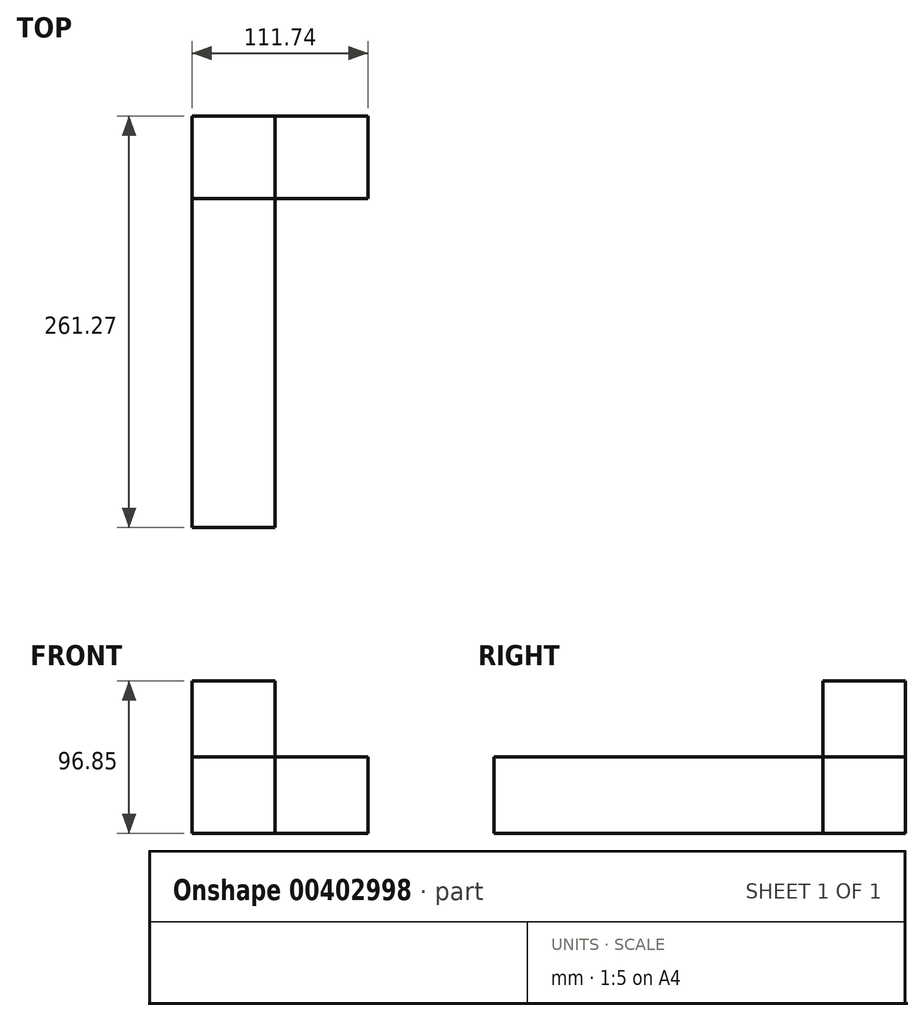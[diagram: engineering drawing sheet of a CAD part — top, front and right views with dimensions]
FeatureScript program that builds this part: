
annotation { "Feature Type Name" : "Feature", "Feature Type Description" : "" }
export const myFeature = defineFeature(function(context is Context, id is Id, definition is map)
    precondition{}
    {
        {
            var Q0;
            Q0=qCreatedBy(makeId("Top.planeOp"),FACE);
            var sketch = newSketch(context, id + "F0", { "sketchPlane" : qUnion([Q0])});
            skLineSegment(sketch, "E0.bottom", {"start": v(0, 0) * mm, "end": v(52.76, 0) * mm});
            skLineSegment(sketch, "E0.top", {"start": v(0, 52.48) * mm, "end": v(52.76, 52.48) * mm});
            skLineSegment(sketch, "E0.left", {"start": v(0, 0) * mm, "end": v(0, 52.48) * mm});
            skLineSegment(sketch, "E0.right", {"start": v(52.76, 0) * mm, "end": v(52.76, 52.48) * mm});
            skSolve(sketch);
        }
        {
            var Q0;
            Q0=makeQuery(id+"F0.imprint","IMPRINT",FACE,{"disambiguationData":[TD([[makeQuery(id+"F0.imprint","IMPRINT",EDGE,{"derivedFrom":sQuery(id+"F0.wireOp",EDGE,"E0.bottom")}),1.0]])]});
            extrude(context, id + "F1", {"entities" : qUnion([Q0]), "depth" : 48.68 * mm});
        }
        {
            var Q0;
            Q0=makeQuery(id+"F1.opExtrude","CAP_FACE",FACE,{"disambiguationData":[OSD([sQuery(id+"F0.wireOp",EDGE,"E0.bottom"),sQuery(id+"F0.wireOp",EDGE,"E0.top"),sQuery(id+"F0.wireOp",EDGE,"E0.left"),sQuery(id+"F0.wireOp",EDGE,"E0.right")])],"isStart":false});
            extrude(context, id + "F2", {"entities" : qUnion([Q0]), "depth" : 48.17 * mm});
        }
        {
            var Q0;
            Q0=makeQuery(id+"F1.opExtrude","SWEPT_FACE",FACE,{"disambiguationData":[OSD([sQuery(id+"F0.wireOp",EDGE,"E0.bottom")])]});
            var sketch = newSketch(context, id + "F3", { "sketchPlane" : qUnion([Q0])});
            skSolve(sketch);
        }
        {
            var Q0;
            {var subQ0=sQuery(id+"F0.wireOp",EDGE,"E0.bottom");Q0=makeQuery(id+"F3.imprint","IMPRINT",FACE,{"disambiguationData":[TD([[makeQuery(id+"F3.imprint","IMPRINT",EDGE,{"derivedFrom":makeQuery(id+"F1.opExtrude","CAP_EDGE",EDGE,{"disambiguationData":[OSD([subQ0])],"isStart":true})}),1.0]])]});}
            extrude(context, id + "F4", {"entities" : qUnion([Q0]), "depth" : 208.8 * mm});
        }
        {
            var Q0;
            Q0=makeQuery(id+"F1.opExtrude","SWEPT_FACE",FACE,{"disambiguationData":[OSD([sQuery(id+"F0.wireOp",EDGE,"E0.right")])]});
            extrude(context, id + "F5", {"entities" : qUnion([Q0]), "depth" : 58.98 * mm});
        }
    });
